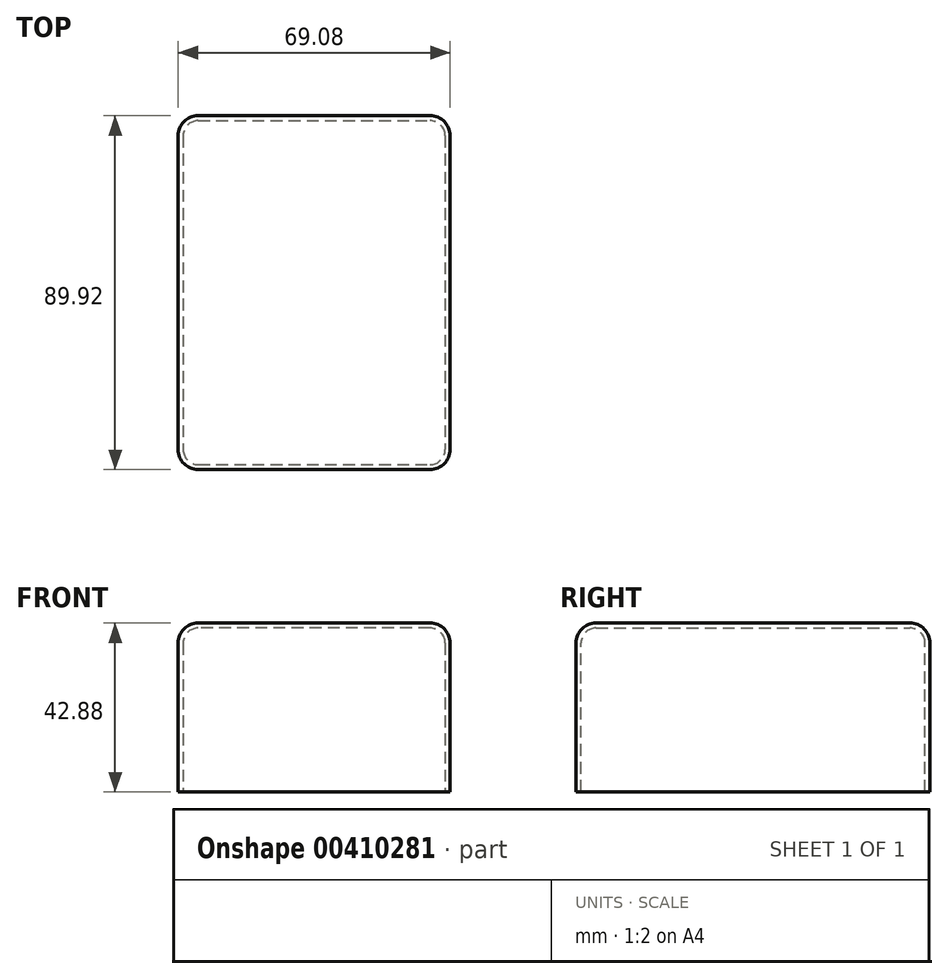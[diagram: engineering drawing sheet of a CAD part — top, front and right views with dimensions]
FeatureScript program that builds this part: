
annotation { "Feature Type Name" : "Feature", "Feature Type Description" : "" }
export const myFeature = defineFeature(function(context is Context, id is Id, definition is map)
    precondition{}
    {
        {
            var Q0;
            Q0=qCreatedBy(makeId("Front.planeOp"),FACE);
            var sketch = newSketch(context, id + "F0", { "sketchPlane" : qUnion([Q0])});
            skLineSegment(sketch, "E0.bottom", {"start": v(-32.03, -17.3) * mm, "end": v(37.05, -17.3) * mm});
            skLineSegment(sketch, "E0.top", {"start": v(-32.03, 25.58) * mm, "end": v(37.05, 25.58) * mm});
            skLineSegment(sketch, "E0.left", {"start": v(-32.03, -17.3) * mm, "end": v(-32.03, 25.58) * mm});
            skLineSegment(sketch, "E0.right", {"start": v(37.05, -17.3) * mm, "end": v(37.05, 25.58) * mm});
            skSolve(sketch);
        }
        {
            var Q0;
            Q0=makeQuery(id+"F0.imprint","IMPRINT",FACE,{"disambiguationData":[TD([[makeQuery(id+"F0.imprint","IMPRINT",EDGE,{"derivedFrom":sQuery(id+"F0.wireOp",EDGE,"E0.bottom")}),1.0]])]});
            extrude(context, id + "F1", {"entities" : qUnion([Q0]), "oppositeDirection" : true, "depth" : 89.92 * mm});
        }
        {
            var Q0;
            Q0=makeQuery(id+"F1.opExtrude","SWEPT_EDGE",EDGE,{"disambiguationData":[OSD([sQuery(id+"F0.wireOp",EDGE,"E0.top"),sQuery(id+"F0.wireOp",EDGE,"E0.right")])]});
            var Q1;
            Q1=makeQuery(id+"F1.opExtrude","CAP_EDGE",EDGE,{"disambiguationData":[OSD([sQuery(id+"F0.wireOp",EDGE,"E0.right")])],"isStart":true});
            var Q2;
            Q2=makeQuery(id+"F1.opExtrude","CAP_EDGE",EDGE,{"disambiguationData":[OSD([sQuery(id+"F0.wireOp",EDGE,"E0.top")])],"isStart":true});
            var Q3;
            Q3=makeQuery(id+"F1.opExtrude","SWEPT_EDGE",EDGE,{"disambiguationData":[OSD([sQuery(id+"F0.wireOp",EDGE,"E0.top"),sQuery(id+"F0.wireOp",EDGE,"E0.left")])]});
            var Q4;
            Q4=makeQuery(id+"F1.opExtrude","CAP_EDGE",EDGE,{"disambiguationData":[OSD([sQuery(id+"F0.wireOp",EDGE,"E0.left")])],"isStart":true});
            var Q5;
            Q5=makeQuery(id+"F1.opExtrude","CAP_EDGE",EDGE,{"disambiguationData":[OSD([sQuery(id+"F0.wireOp",EDGE,"E0.left")])],"isStart":false});
            var Q6;
            Q6=makeQuery(id+"F1.opExtrude","CAP_EDGE",EDGE,{"disambiguationData":[OSD([sQuery(id+"F0.wireOp",EDGE,"E0.right")])],"isStart":false});
            var Q7;
            Q7=makeQuery(id+"F1.opExtrude","CAP_EDGE",EDGE,{"disambiguationData":[OSD([sQuery(id+"F0.wireOp",EDGE,"E0.top")])],"isStart":false});
            fillet(context, id + "F2", {"entities" : qUnion([Q0, Q1, Q2, Q3, Q4, Q5, Q6, Q7]), "radius" : 5.08 * mm, "tangentPropagation" : true, "allowEdgeOverflow" : false});
        }
        {
            var Q0;
            Q0=makeQuery(id+"F1.opExtrude","SWEPT_FACE",FACE,{"disambiguationData":[OSD([sQuery(id+"F0.wireOp",EDGE,"E0.bottom")])]});
            shell(context, id + "F3", {"entities" : qUnion([Q0]), "thickness" : 1.27 * mm});
        }
    });
